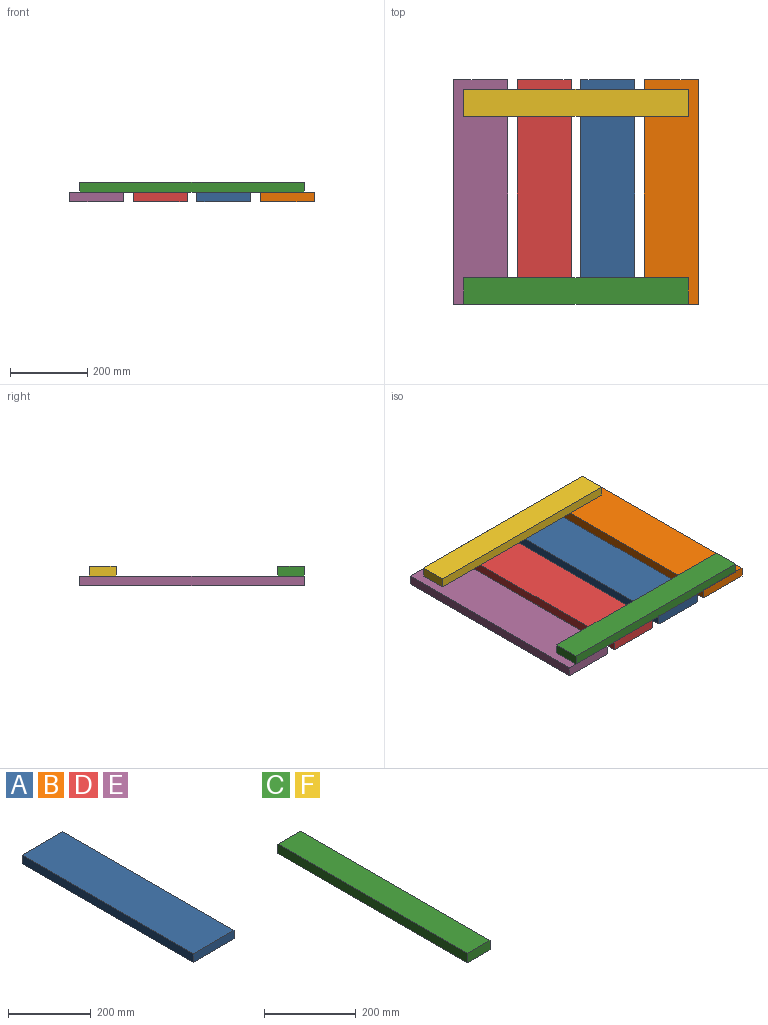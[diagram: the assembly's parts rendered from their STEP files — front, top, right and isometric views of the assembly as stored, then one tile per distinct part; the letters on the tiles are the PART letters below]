
ASSEMBLY  parts=6 mates=2
PART A: 6 faces, bbox 139.7x584.2x25.4 mm
  f0: plane 139.7x25.4mm, normal (0,1,0), area 3548.4mm2, adj f1,f3,f4,f5
  f1: plane 584.2x25.4mm, normal (-1,0,0), area 14838.7mm2, adj f0,f2,f4,f5
  f2: plane 139.7x25.4mm, normal (0,-1,0), area 3548.4mm2, adj f1,f3,f4,f5
  f3: plane 584.2x25.4mm, normal (1,0,0), area 14838.7mm2, adj f0,f2,f4,f5
  f4: plane 584.2x139.7mm, normal (0,0,1), area 81612.7mm2, adj f0,f1,f2,f3
  f5: plane 584.2x139.7mm, normal (0,0,-1), area 81612.7mm2, adj f0,f1,f2,f3
PART B: same geometry as A
PART C: 6 faces, bbox 69.9x584.2x25.4 mm
  f0: plane 69.85x25.4mm, normal (0,1,0), area 1774.2mm2, adj f1,f3,f4,f5
  f1: plane 584.2x25.4mm, normal (-1,0,0), area 14838.7mm2, adj f0,f2,f4,f5
  f2: plane 69.85x25.4mm, normal (0,-1,0), area 1774.2mm2, adj f1,f3,f4,f5
  f3: plane 584.2x25.4mm, normal (1,0,0), area 14838.7mm2, adj f0,f2,f4,f5
  f4: plane 584.2x69.85mm, normal (0,0,1), area 40806.4mm2, adj f0,f1,f2,f3
  f5: plane 584.2x69.85mm, normal (0,0,-1), area 40806.4mm2, adj f0,f1,f2,f3
PART D: same geometry as A
PART E: same geometry as A
PART F: same geometry as C
PLACE A t=(348.02,316.5,-137.76)mm
PLACE B t=(513.12,316.5,-137.76)mm
PLACE C rot(axis=(0,0,-1),90deg) t=(627.42,-197.85,-112.36)mm
PLACE D t=(182.92,316.5,-137.76)mm
PLACE E t=(17.82,316.5,-137.76)mm fixed
PLACE F rot(axis=(0,0,1),90deg) t=(43.22,221.25,-112.36)mm
MATE fastened E.f4 <-> F.f5  axis (0,0,1) through (17.82,316.5,-112.36)mm
MATE fastened E.f4 <-> C.f5  axis (0,0,1) through (17.82,-267.7,-112.36)mm
